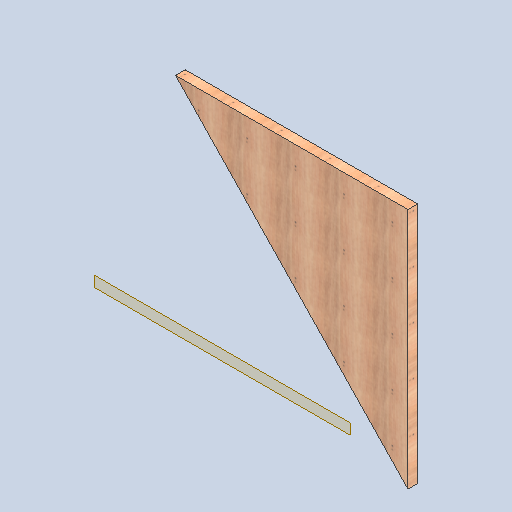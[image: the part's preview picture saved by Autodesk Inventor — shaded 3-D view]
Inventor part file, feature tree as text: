
AUTODESK INVENTOR PART (.ipt)
format: ipt  version: 2025 (Build 290162000, 162)  size: 164,864 bytes
history: native  units: in
note: dims shown in document units (in); Inventor stores cm internally (conversion verified against a paired STEP export)
features: other x5, reference x3, plane x1, extrude x1, sketch x1
ambient origin geometry x8: Origin, YZ Plane, XZ Plane, XY Plane, X Axis, Y Axis, Z Axis, Center Point
bodies: Body1 (feature_tree)
feature tree (11):
  plane  "Work Plane1"
  extrude  "Extrusion3"  Depth=2.0in TaperAngle=0.0deg
  sketch  "Sketch1"  dims[d5=4.0in d6=2.0in d7=0.0in]
  reference  "Reference1"
  reference  "Reference2"
  reference  "Reference3"
  other  "<userpath>\Documents\GitHub\USCTigerBurn24\v2\Tiger.iam"
  other  "Tiger.iam"
  other  "2x4x48:14"
  other  "2x4x48:12"
  other  "2x4x48:9"
